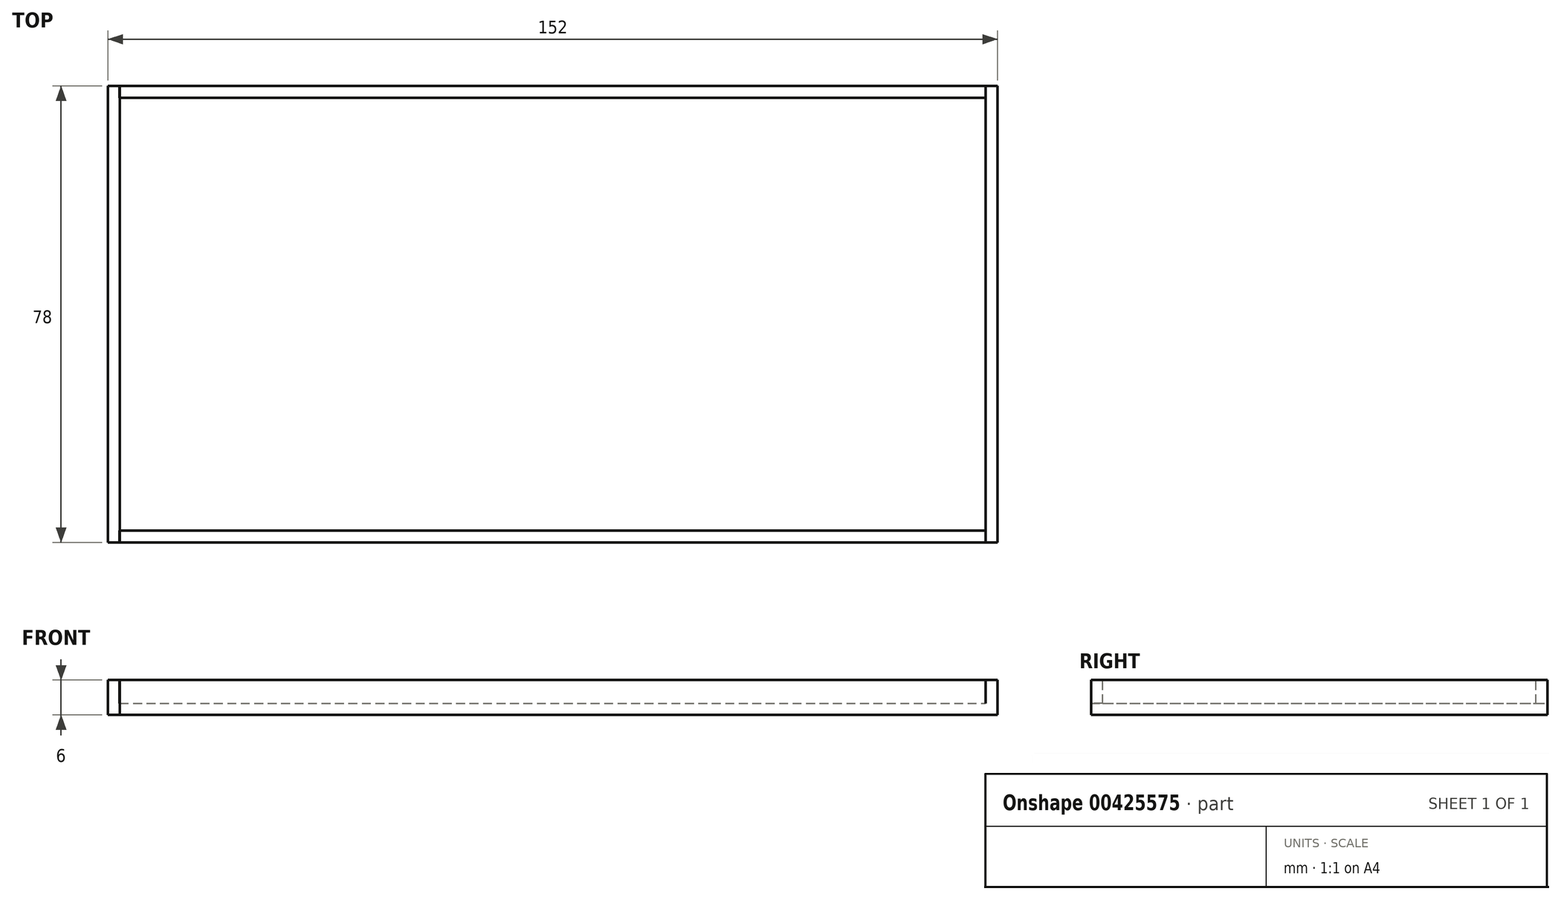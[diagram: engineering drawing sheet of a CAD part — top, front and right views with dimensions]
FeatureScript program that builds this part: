
annotation { "Feature Type Name" : "Feature", "Feature Type Description" : "" }
export const myFeature = defineFeature(function(context is Context, id is Id, definition is map)
    precondition{}
    {
        {
            var Q0;
            Q0=qCreatedBy(makeId("Front.planeOp"),FACE);
            var sketch = newSketch(context, id + "F0", { "sketchPlane" : qUnion([Q0])});
            skLineSegment(sketch, "E0.bottom", {"start": v(-68.42, 0) * mm, "end": v(79.58, 0) * mm});
            skLineSegment(sketch, "E0.top", {"start": v(-68.42, 4) * mm, "end": v(79.58, 4) * mm});
            skLineSegment(sketch, "E0.left", {"start": v(-68.42, 0) * mm, "end": v(-68.42, 4) * mm});
            skLineSegment(sketch, "E0.right", {"start": v(79.58, 0) * mm, "end": v(79.58, 4) * mm});
            skSolve(sketch);
        }
        {
            var Q0;
            Q0=qCreatedBy(makeId("Top.planeOp"),FACE);
            var sketch = newSketch(context, id + "F1", { "sketchPlane" : qUnion([Q0])});
            skLineSegment(sketch, "E1.bottom", {"start": v(-68.4, 0) * mm, "end": v(79.6, 0) * mm});
            skLineSegment(sketch, "E1.top", {"start": v(-68.4, 39) * mm, "end": v(79.6, 39) * mm});
            skLineSegment(sketch, "E1.left", {"start": v(-68.4, 0) * mm, "end": v(-68.4, 39) * mm});
            skLineSegment(sketch, "E1.right", {"start": v(79.6, 0) * mm, "end": v(79.6, 39) * mm});
            skSolve(sketch);
        }
        {
            var Q0;
            Q0 = qSketchRegion(id + "F0", true);
            extrude(context, id + "F2", {"entities" : qUnion([Q0]), "oppositeDirection" : true, "depth" : 2 * mm});
        }
        {
            var Q0;
            Q0 = qSketchRegion(id + "F1", true);
            extrude(context, id + "F3", {"entities" : qUnion([Q0]), "depth" : -2 * mm});
        }
        {
            var Q0;
            Q0=makeQuery(id+"F3.opExtrude","SWEPT_BODY",BODY,{"disambiguationData":[OSD([sQuery(id+"F1.wireOp",EDGE,"E1.bottom"),sQuery(id+"F1.wireOp",EDGE,"E1.top"),sQuery(id+"F1.wireOp",EDGE,"E1.left"),sQuery(id+"F1.wireOp",EDGE,"E1.right")])]});
            var Q1;
            Q1=makeQuery(id+"F2.opExtrude","SWEPT_BODY",BODY,{"disambiguationData":[OSD([sQuery(id+"F0.wireOp",EDGE,"E0.bottom"),sQuery(id+"F0.wireOp",EDGE,"E0.top"),sQuery(id+"F0.wireOp",EDGE,"E0.left"),sQuery(id+"F0.wireOp",EDGE,"E0.right")])]});
            var Q2;
            Q2=makeQuery(id+"F3.opExtrude","SWEPT_FACE",FACE,{"disambiguationData":[OSD([sQuery(id+"F1.wireOp",EDGE,"E1.top")])]});
            mirror(context, id + "F4", {"operationType" : NewBodyOperationType.ADD, "entities" : qUnion([Q0, Q1]), "mirrorPlane" : qUnion([Q2])});
        }
        {
            var Q0;
            {var subQ0=makeQuery(id+"F3.opExtrude","SWEPT_FACE",FACE,{"disambiguationData":[OSD([sQuery(id+"F1.wireOp",EDGE,"E1.left")])]});Q0=makeQuery(id+"F4.boolean.opBoolean","MERGE",FACE,{"derivedFrom":[subQ0,makeQuery(id+"F4.opPattern","COPY",FACE,{"derivedFrom":subQ0,"instanceName":"1"})]});}
            var sketch = newSketch(context, id + "F5", { "sketchPlane" : qUnion([Q0])});
            skLineSegment(sketch, "E2.bottom", {"start": v(-78, 4) * mm, "end": v(0, 4) * mm});
            skLineSegment(sketch, "E2.top", {"start": v(-78, -2) * mm, "end": v(0, -2) * mm});
            skLineSegment(sketch, "E2.left", {"start": v(-78, 4) * mm, "end": v(-78, -2) * mm});
            skLineSegment(sketch, "E2.right", {"start": v(0, 4) * mm, "end": v(0, -2) * mm});
            skSolve(sketch);
        }
        {
            var Q0;
            Q0 = qSketchRegion(id + "F5", true);
            extrude(context, id + "F6", {"entities" : qUnion([Q0]), "depth" : 2 * mm});
        }
        {
            var Q0;
            {var subQ0=makeQuery(id+"F3.opExtrude","SWEPT_FACE",FACE,{"disambiguationData":[OSD([sQuery(id+"F1.wireOp",EDGE,"E1.right")])]});Q0=makeQuery(id+"F4.boolean.opBoolean","MERGE",FACE,{"derivedFrom":[subQ0,makeQuery(id+"F4.opPattern","COPY",FACE,{"derivedFrom":subQ0,"instanceName":"1"})]});}
            var sketch = newSketch(context, id + "F7", { "sketchPlane" : qUnion([Q0])});
            skLineSegment(sketch, "E3.bottom", {"start": v(0, 4) * mm, "end": v(78, 4) * mm});
            skLineSegment(sketch, "E3.top", {"start": v(0, -2) * mm, "end": v(78, -2) * mm});
            skLineSegment(sketch, "E3.left", {"start": v(0, 4) * mm, "end": v(0, -2) * mm});
            skLineSegment(sketch, "E3.right", {"start": v(78, 4) * mm, "end": v(78, -2) * mm});
            skSolve(sketch);
        }
        {
            var Q0;
            Q0 = qSketchRegion(id + "F7", true);
            extrude(context, id + "F8", {"entities" : qUnion([Q0]), "operationType" : NewBodyOperationType.ADD, "depth" : 2 * mm});
        }
    });
